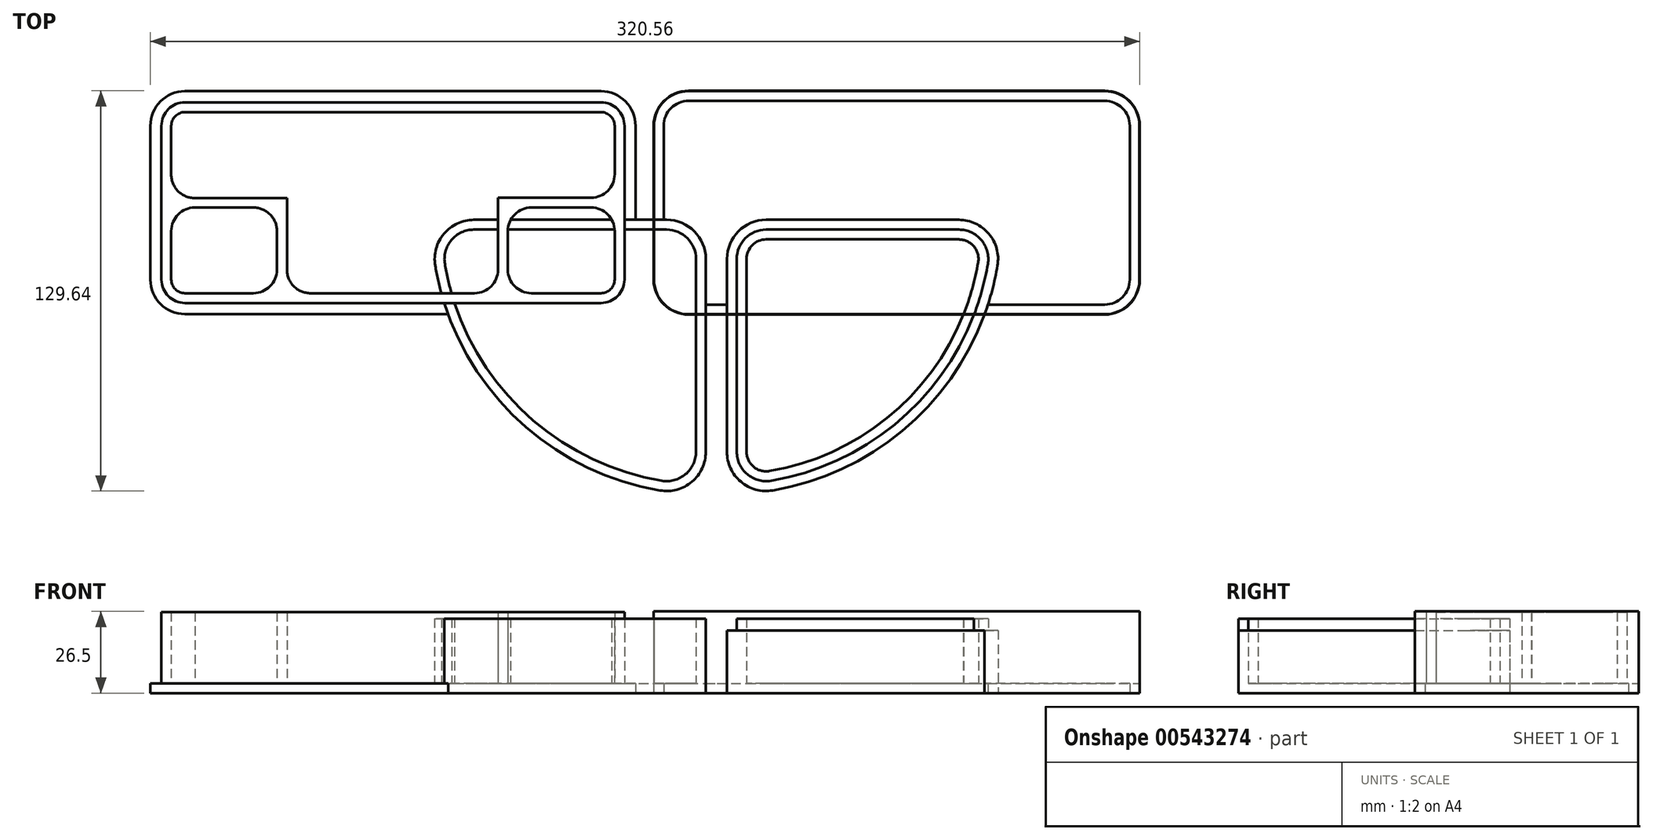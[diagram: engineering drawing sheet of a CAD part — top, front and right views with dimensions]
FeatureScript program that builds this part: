
annotation { "Feature Type Name" : "Feature", "Feature Type Description" : "" }
export const myFeature = defineFeature(function(context is Context, id is Id, definition is map)
    precondition{}
    {
        {
            var Q0;
            Q0=qCreatedBy(makeId("Top.planeOp"),FACE);
            var sketch = newSketch(context, id + "F0", { "sketchPlane" : qUnion([Q0])});
            skLineSegment(sketch, "E0.bottom", {"start": v(10.47, 17.5) * mm, "end": v(-124.29, 17.5) * mm});
            skLineSegment(sketch, "E0.top", {"start": v(10.47, 82.5) * mm, "end": v(-124.29, 82.5) * mm});
            skLineSegment(sketch, "E0.left", {"start": v(18.1, 25.13) * mm, "end": v(18.1, 74.89) * mm});
            skLineSegment(sketch, "E0.right", {"start": v(-131.9, 25.13) * mm, "end": v(-131.9, 74.89) * mm});
            skPoint(sketch, "E0.middle", {"position": v(-56.9, 50) * mm});
            skPoint(sketch, "E1.visualSharp", {"position": v(-131.9, 82.5) * mm});
            skArc(sketch, "E1.filletArc", {"start": v(-124.29, 82.5) * mm, "mid": v(-129.68, 80.28) * mm, "end": v(-131.9, 74.89) * mm});
            skPoint(sketch, "E2.visualSharp", {"position": v(-131.9, 17.5) * mm});
            skArc(sketch, "E2.filletArc", {"start": v(-131.9, 25.13) * mm, "mid": v(-129.68, 19.74) * mm, "end": v(-124.29, 17.5) * mm});
            skPoint(sketch, "E3.visualSharp", {"position": v(18.1, 17.5) * mm});
            skArc(sketch, "E3.filletArc", {"start": v(10.47, 17.5) * mm, "mid": v(15.86, 19.74) * mm, "end": v(18.1, 25.13) * mm});
            skPoint(sketch, "E4.visualSharp", {"position": v(18.1, 82.5) * mm});
            skArc(sketch, "E4.filletArc", {"start": v(18.1, 74.89) * mm, "mid": v(15.86, 80.28) * mm, "end": v(10.47, 82.5) * mm});
            skArc(sketch, "E5.0", {"start": v(14.92, 74.89) * mm, "mid": v(13.61, 78.03) * mm, "end": v(10.47, 79.33) * mm});
            skLineSegment(sketch, "E5.1", {"start": v(14.92, 59.22) * mm, "end": v(14.92, 74.89) * mm});
            skLineSegment(sketch, "E5.2", {"start": v(10.47, 79.33) * mm, "end": v(-124.29, 79.33) * mm});
            skArc(sketch, "E5.3", {"start": v(10.47, 20.68) * mm, "mid": v(13.61, 21.98) * mm, "end": v(14.92, 25.13) * mm});
            skArc(sketch, "E5.4", {"start": v(-124.29, 79.33) * mm, "mid": v(-127.43, 78.03) * mm, "end": v(-128.73, 74.89) * mm});
            skLineSegment(sketch, "E5.5", {"start": v(-128.73, 59.11) * mm, "end": v(-128.73, 74.89) * mm});
            skArc(sketch, "E5.6", {"start": v(-128.73, 25.13) * mm, "mid": v(-127.43, 21.98) * mm, "end": v(-124.29, 20.68) * mm});
            skLineSegment(sketch, "E5.7", {"start": v(-30.47, 20.68) * mm, "end": v(-83.6, 20.68) * mm});
            skLineSegment(sketch, "E6.0", {"start": v(24.7, 25.13) * mm, "end": v(24.7, 74.89) * mm, "construction": true});
            skLineSegment(sketch, "E7.left", {"start": v(14.92, 40.8) * mm, "end": v(14.92, 59.22) * mm});
            skLineSegment(sketch, "E7.right", {"start": v(-128.73, 49.97) * mm, "end": v(-128.73, 51.6) * mm});
            skPoint(sketch, "E8.newPointA", {"position": v(-128.73, 51.6) * mm});
            skPoint(sketch, "E8.newPointB", {"position": v(-128.73, 25.13) * mm});
            skArc(sketch, "E8.filletArc", {"start": v(-128.73, 59.11) * mm, "mid": v(-126.47, 53.7) * mm, "end": v(-121.01, 51.5) * mm});
            skPoint(sketch, "E9.newPointA", {"position": v(14.92, 51.6) * mm});
            skPoint(sketch, "E9.newPointB", {"position": v(14.92, 25.13) * mm});
            skArc(sketch, "E9.filletArc", {"start": v(7.3, 51.6) * mm, "mid": v(12.68, 53.83) * mm, "end": v(14.92, 59.22) * mm});
            skPoint(sketch, "E10.visualSharp", {"position": v(-128.73, 48.42) * mm});
            skLineSegment(sketch, "E11", {"start": v(-128.73, 25.13) * mm, "end": v(-128.73, 40.8) * mm});
            skLineSegment(sketch, "E12", {"start": v(14.92, 25.13) * mm, "end": v(14.92, 40.8) * mm});
            skArc(sketch, "E13.filletArc", {"start": v(-121.11, 48.42) * mm, "mid": v(-126.5, 46.19) * mm, "end": v(-128.73, 40.8) * mm});
            skPoint(sketch, "E14.visualSharp", {"position": v(14.92, 48.42) * mm});
            skArc(sketch, "E14.filletArc", {"start": v(14.92, 40.8) * mm, "mid": v(12.68, 46.19) * mm, "end": v(7.3, 48.42) * mm});
            skLineSegment(sketch, "E15", {"start": v(-128.73, 59.11) * mm, "end": v(-128.73, 40.8) * mm});
            skArc(sketch, "E16.0", {"start": v(27.55, 74.89) * mm, "mid": v(30.88, 82.93) * mm, "end": v(38.92, 86.26) * mm});
            skLineSegment(sketch, "E16.1", {"start": v(27.55, 25.13) * mm, "end": v(27.55, 74.89) * mm});
            skLineSegment(sketch, "E16.2", {"start": v(38.92, 86.26) * mm, "end": v(173.68, 86.26) * mm});
            skArc(sketch, "E16.3", {"start": v(38.92, 13.76) * mm, "mid": v(30.88, 17.09) * mm, "end": v(27.55, 25.13) * mm});
            skArc(sketch, "E16.4", {"start": v(173.68, 86.26) * mm, "mid": v(181.72, 82.93) * mm, "end": v(185.05, 74.89) * mm});
            skLineSegment(sketch, "E16.5", {"start": v(185.05, 25.13) * mm, "end": v(185.05, 74.89) * mm});
            skArc(sketch, "E16.6", {"start": v(185.05, 25.13) * mm, "mid": v(181.72, 17.09) * mm, "end": v(173.68, 13.76) * mm});
            skLineSegment(sketch, "E16.7", {"start": v(38.92, 13.76) * mm, "end": v(173.68, 13.76) * mm});
            skArc(sketch, "E17.0", {"start": v(27.65, 74.89) * mm, "mid": v(30.95, 82.86) * mm, "end": v(38.92, 86.16) * mm});
            skLineSegment(sketch, "E17.1", {"start": v(27.65, 25.13) * mm, "end": v(27.65, 74.89) * mm});
            skLineSegment(sketch, "E17.2", {"start": v(38.92, 86.16) * mm, "end": v(173.68, 86.16) * mm});
            skArc(sketch, "E17.3", {"start": v(38.92, 13.86) * mm, "mid": v(30.95, 17.16) * mm, "end": v(27.65, 25.13) * mm});
            skArc(sketch, "E17.4", {"start": v(173.68, 86.16) * mm, "mid": v(181.65, 82.86) * mm, "end": v(184.95, 74.89) * mm});
            skLineSegment(sketch, "E17.5", {"start": v(184.95, 25.13) * mm, "end": v(184.95, 74.89) * mm});
            skArc(sketch, "E17.6", {"start": v(184.95, 25.13) * mm, "mid": v(181.65, 17.16) * mm, "end": v(173.68, 13.86) * mm});
            skLineSegment(sketch, "E17.7", {"start": v(38.92, 13.86) * mm, "end": v(173.68, 13.86) * mm});
            skArc(sketch, "E18.0", {"start": v(30.8, 74.89) * mm, "mid": v(33.18, 80.63) * mm, "end": v(38.92, 83) * mm});
            skLineSegment(sketch, "E18.1", {"start": v(30.8, 25.13) * mm, "end": v(30.8, 74.89) * mm});
            skLineSegment(sketch, "E18.2", {"start": v(38.92, 83) * mm, "end": v(173.68, 83) * mm});
            skArc(sketch, "E18.3", {"start": v(38.92, 17) * mm, "mid": v(33.18, 19.39) * mm, "end": v(30.8, 25.13) * mm});
            skArc(sketch, "E18.4", {"start": v(173.68, 83) * mm, "mid": v(179.42, 80.63) * mm, "end": v(181.8, 74.89) * mm});
            skLineSegment(sketch, "E18.5", {"start": v(181.8, 25.13) * mm, "end": v(181.8, 74.89) * mm});
            skArc(sketch, "E18.6", {"start": v(181.8, 25.13) * mm, "mid": v(179.42, 19.39) * mm, "end": v(173.68, 17) * mm});
            skLineSegment(sketch, "E18.7", {"start": v(38.92, 17) * mm, "end": v(173.68, 17) * mm});
            skLineSegment(sketch, "E19.1.0.0", {"start": v(-94.5, 28.3) * mm, "end": v(-94.48, 40.79) * mm});
            skPoint(sketch, "E20.orphan", {"position": v(-92.9, 40.77) * mm});
            skPoint(sketch, "E21.orphan", {"position": v(-57.07, 40.74) * mm});
            skPoint(sketch, "E22.orphan", {"position": v(-21.23, 40.72) * mm});
            skPoint(sketch, "E23.orphan", {"position": v(-21.23, 25.04) * mm});
            skPoint(sketch, "E24.orphan", {"position": v(-57.07, 25.07) * mm});
            skArc(sketch, "E25.filletArc", {"start": v(-91.23, 28.32) * mm, "mid": v(-89, 22.92) * mm, "end": v(-83.6, 20.68) * mm});
            skArc(sketch, "E26.filletArc", {"start": v(-30.47, 20.68) * mm, "mid": v(-25.08, 22.91) * mm, "end": v(-22.85, 28.3) * mm});
            skLineSegment(sketch, "E27", {"start": v(-124.29, 20.68) * mm, "end": v(-102.12, 20.68) * mm});
            skLineSegment(sketch, "E28", {"start": v(-12.05, 20.68) * mm, "end": v(10.47, 20.68) * mm});
            skLineSegment(sketch, "E29", {"start": v(-12.05, 48.42) * mm, "end": v(7.3, 48.42) * mm});
            skPoint(sketch, "E30.visualSharp", {"position": v(-19.67, 48.42) * mm});
            skArc(sketch, "E30.filletArc", {"start": v(-12.05, 48.42) * mm, "mid": v(-17.44, 46.19) * mm, "end": v(-19.67, 40.8) * mm});
            skPoint(sketch, "E31.visualSharp", {"position": v(-19.67, 20.68) * mm});
            skArc(sketch, "E31.filletArc", {"start": v(-19.67, 28.3) * mm, "mid": v(-17.44, 22.91) * mm, "end": v(-12.05, 20.68) * mm});
            skPoint(sketch, "E32.visualSharp", {"position": v(-94.51, 20.68) * mm});
            skArc(sketch, "E32.filletArc", {"start": v(-102.12, 20.68) * mm, "mid": v(-96.74, 22.91) * mm, "end": v(-94.5, 28.3) * mm});
            skLineSegment(sketch, "E33", {"start": v(-121.11, 48.42) * mm, "end": v(-102.1, 48.42) * mm});
            skArc(sketch, "E34.filletArc", {"start": v(-94.48, 40.79) * mm, "mid": v(-96.7, 46.18) * mm, "end": v(-102.1, 48.42) * mm});
            skLineSegment(sketch, "E35", {"start": v(7.3, 51.6) * mm, "end": v(-121.01, 51.5) * mm});
            skLineSegment(sketch, "E36", {"start": v(-22.85, 28.3) * mm, "end": v(-22.87, 51.57) * mm});
            skLineSegment(sketch, "E37", {"start": v(-91.23, 28.32) * mm, "end": v(-91.24, 51.52) * mm});
            skLineSegment(sketch, "E38", {"start": v(-19.67, 28.3) * mm, "end": v(-19.67, 40.8) * mm});
            skLineSegment(sketch, "E39", {"start": v(42.8, 86.16) * mm, "end": v(-129, 86.16) * mm, "construction": true});
            skArc(sketch, "E40.0", {"start": v(21.7, 74.89) * mm, "mid": v(18.4, 82.82) * mm, "end": v(10.47, 86.1) * mm});
            skLineSegment(sketch, "E40.1", {"start": v(21.7, 25.13) * mm, "end": v(21.7, 74.89) * mm});
            skLineSegment(sketch, "E40.2", {"start": v(10.47, 86.1) * mm, "end": v(-124.29, 86.1) * mm});
            skArc(sketch, "E40.3", {"start": v(10.47, 13.9) * mm, "mid": v(18.4, 17.2) * mm, "end": v(21.7, 25.13) * mm});
            skArc(sketch, "E40.4", {"start": v(-124.29, 86.1) * mm, "mid": v(-132.22, 82.82) * mm, "end": v(-135.5, 74.89) * mm});
            skLineSegment(sketch, "E40.5", {"start": v(-135.5, 25.13) * mm, "end": v(-135.5, 74.89) * mm});
            skArc(sketch, "E40.6", {"start": v(-135.5, 25.13) * mm, "mid": v(-132.22, 17.2) * mm, "end": v(-124.29, 13.9) * mm});
            skLineSegment(sketch, "E40.7", {"start": v(10.47, 13.9) * mm, "end": v(-124.29, 13.9) * mm});
            skSolve(sketch);
        }
        {
            var Q0;
            Q0=qCreatedBy(makeId("Top.planeOp"),FACE);
            var sketch = newSketch(context, id + "F1", { "sketchPlane" : qUnion([Q0])});
            skLineSegment(sketch, "E41.bottom", {"start": v(44.45, -44.45) * mm, "end": v(-44.45, -44.45) * mm});
            skLineSegment(sketch, "E41.top", {"start": v(31.75, 44.45) * mm, "end": v(-30.68, 44.45) * mm});
            skLineSegment(sketch, "E41.left", {"start": v(44.45, -30.68) * mm, "end": v(44.45, 31.75) * mm});
            skLineSegment(sketch, "E41.right", {"start": v(-44.45, -44.45) * mm, "end": v(-44.45, 44.45) * mm});
            skPoint(sketch, "E41.middle", {"position": v(0, 0) * mm});
            skLineSegment(sketch, "E42.0", {"start": v(47.88, -44.45) * mm, "end": v(47.88, 44.45) * mm, "construction": true});
            skArc(sketch, "E43", {"start": v(-43.2, 29.63) * mm, "mid": v(-18.41, -18.41) * mm, "end": v(29.63, -43.2) * mm});
            skPoint(sketch, "E44.visualSharp", {"position": v(-44.45, 44.45) * mm});
            skArc(sketch, "E44.filletArc", {"start": v(-30.68, 44.45) * mm, "mid": v(-40.38, 39.95) * mm, "end": v(-43.2, 29.63) * mm});
            skPoint(sketch, "E45.visualSharp", {"position": v(44.45, -44.45) * mm});
            skArc(sketch, "E45.filletArc", {"start": v(29.63, -43.2) * mm, "mid": v(39.95, -40.38) * mm, "end": v(44.45, -30.68) * mm});
            skArc(sketch, "E46.filletArc", {"start": v(44.45, 31.75) * mm, "mid": v(40.73, 40.73) * mm, "end": v(31.75, 44.45) * mm});
            skArc(sketch, "E47.0", {"start": v(41.28, 31.75) * mm, "mid": v(38.49, 38.49) * mm, "end": v(31.75, 41.27) * mm});
            skArc(sketch, "E47.1", {"start": v(-30.68, 41.27) * mm, "mid": v(-37.96, 37.9) * mm, "end": v(-40.08, 30.16) * mm});
            skArc(sketch, "E47.2", {"start": v(-40.08, 30.16) * mm, "mid": v(-16.17, -16.17) * mm, "end": v(30.16, -40.08) * mm});
            skLineSegment(sketch, "E47.3", {"start": v(31.75, 41.27) * mm, "end": v(-30.68, 41.27) * mm});
            skArc(sketch, "E47.4", {"start": v(30.16, -40.08) * mm, "mid": v(37.9, -37.96) * mm, "end": v(41.28, -30.68) * mm});
            skLineSegment(sketch, "E47.5", {"start": v(41.28, -30.68) * mm, "end": v(41.28, 31.75) * mm});
            skLineSegment(sketch, "E48.0", {"start": v(31.75, 38.1) * mm, "end": v(-30.68, 38.1) * mm});
            skArc(sketch, "E48.1", {"start": v(-36.95, 30.7) * mm, "mid": v(-13.92, -13.92) * mm, "end": v(30.7, -36.95) * mm});
            skArc(sketch, "E48.2", {"start": v(30.7, -36.95) * mm, "mid": v(35.85, -35.53) * mm, "end": v(38.1, -30.68) * mm});
            skArc(sketch, "E48.3", {"start": v(-30.68, 38.1) * mm, "mid": v(-35.53, 35.85) * mm, "end": v(-36.95, 30.7) * mm});
            skLineSegment(sketch, "E48.4", {"start": v(38.1, -30.68) * mm, "end": v(38.1, 31.75) * mm});
            skArc(sketch, "E48.5", {"start": v(38.1, 31.75) * mm, "mid": v(36.24, 36.24) * mm, "end": v(31.75, 38.1) * mm});
            skLineSegment(sketch, "E49.MirrorCS", {"start": v(51.3, -30.68) * mm, "end": v(51.3, 31.75) * mm});
            skLineSegment(sketch, "E50.MirrorCS", {"start": v(54.48, -30.68) * mm, "end": v(54.48, 31.75) * mm});
            skLineSegment(sketch, "E51.MirrorCS", {"start": v(57.66, -30.68) * mm, "end": v(57.66, 31.75) * mm});
            skArc(sketch, "E52.MirrorCS", {"start": v(57.66, 31.75) * mm, "mid": v(59.52, 36.24) * mm, "end": v(64, 38.1) * mm});
            skArc(sketch, "E53.MirrorCS", {"start": v(54.48, 31.75) * mm, "mid": v(57.27, 38.49) * mm, "end": v(64, 41.28) * mm});
            skArc(sketch, "E54.MirrorCS", {"start": v(51.3, 31.75) * mm, "mid": v(55.03, 40.73) * mm, "end": v(64, 44.45) * mm});
            skLineSegment(sketch, "E55.MirrorCS", {"start": v(64, 44.45) * mm, "end": v(126.44, 44.45) * mm});
            skLineSegment(sketch, "E56.MirrorCS", {"start": v(64, 41.27) * mm, "end": v(126.44, 41.27) * mm});
            skLineSegment(sketch, "E57.MirrorCS", {"start": v(64, 38.1) * mm, "end": v(126.44, 38.1) * mm});
            skArc(sketch, "E58.MirrorCS", {"start": v(126.44, 38.1) * mm, "mid": v(131.3, 35.85) * mm, "end": v(132.7, 30.7) * mm});
            skArc(sketch, "E59.MirrorCS", {"start": v(126.44, 41.28) * mm, "mid": v(133.72, 37.9) * mm, "end": v(135.83, 30.16) * mm});
            skArc(sketch, "E60.MirrorCS", {"start": v(126.44, 44.45) * mm, "mid": v(136.14, 39.95) * mm, "end": v(138.96, 29.63) * mm});
            skArc(sketch, "E61.MirrorCS", {"start": v(132.7, 30.7) * mm, "mid": v(109.68, -13.92) * mm, "end": v(65.07, -36.95) * mm});
            skArc(sketch, "E62.MirrorCS", {"start": v(135.83, 30.16) * mm, "mid": v(111.92, -16.17) * mm, "end": v(65.6, -40.08) * mm});
            skArc(sketch, "E63.MirrorCS", {"start": v(138.96, 29.63) * mm, "mid": v(114.17, -18.41) * mm, "end": v(66.12, -43.2) * mm});
            skArc(sketch, "E64.MirrorCS", {"start": v(66.12, -43.2) * mm, "mid": v(55.81, -40.38) * mm, "end": v(51.3, -30.68) * mm});
            skArc(sketch, "E65.MirrorCS", {"start": v(65.6, -40.08) * mm, "mid": v(57.86, -37.96) * mm, "end": v(54.48, -30.68) * mm});
            skArc(sketch, "E66.MirrorCS", {"start": v(65.07, -36.95) * mm, "mid": v(59.9, -35.53) * mm, "end": v(57.66, -30.68) * mm});
            skSolve(sketch);
        }
        {
            var Q0;
            Q0=makeQuery(id+"F1.imprint","IMPRINT",FACE,{"disambiguationData":[TD([[makeQuery(id+"F1.imprint","IMPRINT",EDGE,{"derivedFrom":sQuery(id+"F1.wireOp",EDGE,"E48.0")}),1.0]])]});
            var Q1;
            Q1=makeQuery(id+"F1.imprint","IMPRINT",FACE,{"disambiguationData":[TD([[makeQuery(id+"F1.imprint","IMPRINT",EDGE,{"derivedFrom":sQuery(id+"F1.wireOp",EDGE,"E47.0")}),1.0]])]});
            var Q2;
            Q2=makeQuery(id+"F1.imprint","IMPRINT",FACE,{"disambiguationData":[TD([[makeQuery(id+"F1.imprint","IMPRINT",EDGE,{"derivedFrom":sQuery(id+"F1.wireOp",EDGE,"E41.top")}),1.0]])]});
            var Q3;
            Q3=makeQuery(id+"F1.imprint","IMPRINT",FACE,{"disambiguationData":[TD([[makeQuery(id+"F1.imprint","IMPRINT",EDGE,{"derivedFrom":sQuery(id+"F1.wireOp",EDGE,"E49.MirrorCS")}),-1.0]])]});
            var Q4;
            Q4=makeQuery(id+"F1.imprint","IMPRINT",FACE,{"disambiguationData":[TD([[makeQuery(id+"F1.imprint","IMPRINT",EDGE,{"derivedFrom":sQuery(id+"F1.wireOp",EDGE,"E50.MirrorCS")}),-1.0]])]});
            var Q5;
            Q5=makeQuery(id+"F1.imprint","IMPRINT",FACE,{"disambiguationData":[TD([[makeQuery(id+"F1.imprint","IMPRINT",EDGE,{"derivedFrom":sQuery(id+"F1.wireOp",EDGE,"E51.MirrorCS")}),-1.0]])]});
            extrude(context, id + "F2", {"entities" : qUnion([Q0, Q1, Q2, Q3, Q4, Q5]), "depth" : 3.17 * mm, "offsetDistance" : 25.4 * mm});
        }
        {
            var Q0;
            Q0=makeQuery(id+"F1.imprint","IMPRINT",FACE,{"disambiguationData":[TD([[makeQuery(id+"F1.imprint","IMPRINT",EDGE,{"derivedFrom":sQuery(id+"F1.wireOp",EDGE,"E41.top")}),1.0]])]});
            extrude(context, id + "F3", {"entities" : qUnion([Q0]), "operationType" : NewBodyOperationType.ADD, "depth" : 24.13 * mm, "offsetDistance" : 25.4 * mm});
        }
        {
            var Q0;
            Q0=makeQuery(id+"F1.imprint","IMPRINT",FACE,{"disambiguationData":[TD([[makeQuery(id+"F1.imprint","IMPRINT",EDGE,{"derivedFrom":sQuery(id+"F1.wireOp",EDGE,"E49.MirrorCS")}),-1.0]])]});
            var Q1;
            Q1=makeQuery(id+"F1.imprint","IMPRINT",FACE,{"disambiguationData":[TD([[makeQuery(id+"F1.imprint","IMPRINT",EDGE,{"derivedFrom":sQuery(id+"F1.wireOp",EDGE,"E50.MirrorCS")}),-1.0]])]});
            extrude(context, id + "F4", {"entities" : qUnion([Q0, Q1]), "operationType" : NewBodyOperationType.ADD, "depth" : 20.32 * mm, "offsetDistance" : 25.4 * mm});
        }
        {
            var Q0;
            Q0=makeQuery(id+"F1.imprint","IMPRINT",FACE,{"disambiguationData":[TD([[makeQuery(id+"F1.imprint","IMPRINT",EDGE,{"derivedFrom":sQuery(id+"F1.wireOp",EDGE,"E50.MirrorCS")}),-1.0]])]});
            extrude(context, id + "F5", {"entities" : qUnion([Q0]), "operationType" : NewBodyOperationType.ADD, "depth" : 24.13 * mm, "offsetDistance" : 25.4 * mm});
        }
        {
            var Q0;
            Q0=makeQuery(id+"F0.imprint","IMPRINT",FACE,{"disambiguationData":[TD([[makeQuery(id+"F0.imprint","IMPRINT",EDGE,{"derivedFrom":sQuery(id+"F0.wireOp",EDGE,"E18.0")}),-1.0]])]});
            var Q1;
            Q1=makeQuery(id+"F0.imprint","IMPRINT",FACE,{"disambiguationData":[TD([[makeQuery(id+"F0.imprint","IMPRINT",EDGE,{"derivedFrom":sQuery(id+"F0.wireOp",EDGE,"E17.0")}),-1.0]])]});
            var Q2;
            Q2=makeQuery(id+"F0.imprint","IMPRINT",FACE,{"disambiguationData":[TD([[makeQuery(id+"F0.imprint","IMPRINT",EDGE,{"derivedFrom":sQuery(id+"F0.wireOp",EDGE,"E0.bottom")}),-1.0]])]});
            var Q3;
            Q3=makeQuery(id+"F0.imprint","IMPRINT",FACE,{"disambiguationData":[TD([[makeQuery(id+"F0.imprint","IMPRINT",EDGE,{"derivedFrom":sQuery(id+"F0.wireOp",EDGE,"E5.3")}),1.0]])]});
            var Q4;
            Q4=makeQuery(id+"F0.imprint","IMPRINT",FACE,{"disambiguationData":[TD([[makeQuery(id+"F0.imprint","IMPRINT",EDGE,{"derivedFrom":sQuery(id+"F0.wireOp",EDGE,"E7.bottom")}),-1.0]])]});
            var Q5;
            Q5=makeQuery(id+"F0.imprint","IMPRINT",FACE,{"disambiguationData":[TD([[makeQuery(id+"F0.imprint","IMPRINT",EDGE,{"derivedFrom":sQuery(id+"F0.wireOp",EDGE,"E5.0")}),1.0]])]});
            var Q6;
            Q6=makeQuery(id+"F0.imprint","IMPRINT",FACE,{"disambiguationData":[TD([[makeQuery(id+"F0.imprint","IMPRINT",EDGE,{"derivedFrom":sQuery(id+"F0.wireOp",EDGE,"E5.6")}),1.0]])]});
            var Q7;
            Q7=makeQuery(id+"F0.imprint","IMPRINT",FACE,{"disambiguationData":[TD([[makeQuery(id+"F0.imprint","IMPRINT",EDGE,{"derivedFrom":sQuery(id+"F0.wireOp",EDGE,"E5.7")}),-1.0]])]});
            extrude(context, id + "F6", {"entities" : qUnion([Q0, Q1, Q2, Q3, Q4, Q5, Q6, Q7]), "depth" : 3.17 * mm, "offsetDistance" : 25 * mm});
        }
        {
            var Q0;
            Q0=makeQuery(id+"F0.imprint","IMPRINT",FACE,{"disambiguationData":[TD([[makeQuery(id+"F0.imprint","IMPRINT",EDGE,{"derivedFrom":sQuery(id+"F0.wireOp",EDGE,"E0.bottom")}),-1.0]])]});
            var Q1;
            Q1=makeQuery(id+"F0.imprint","IMPRINT",FACE,{"disambiguationData":[TD([[makeQuery(id+"F0.imprint","IMPRINT",EDGE,{"derivedFrom":sQuery(id+"F0.wireOp",EDGE,"E7.bottom")}),-1.0]])]});
            extrude(context, id + "F7", {"entities" : qUnion([Q0, Q1]), "operationType" : NewBodyOperationType.ADD, "depth" : 26.27 * mm, "offsetDistance" : 25 * mm});
        }
        {
            var Q0;
            Q0=makeQuery(id+"F0.imprint","IMPRINT",FACE,{"disambiguationData":[TD([[makeQuery(id+"F0.imprint","IMPRINT",EDGE,{"derivedFrom":sQuery(id+"F0.wireOp",EDGE,"E17.0")}),-1.0]])]});
            extrude(context, id + "F8", {"entities" : qUnion([Q0]), "operationType" : NewBodyOperationType.ADD, "depth" : 26.5 * mm, "offsetDistance" : 25 * mm});
        }
        {
            var Q0;
            Q0=makeQuery(id+"F0.imprint","IMPRINT",FACE,{"disambiguationData":[TD([[makeQuery(id+"F0.imprint","IMPRINT",EDGE,{"derivedFrom":sQuery(id+"F0.wireOp",EDGE,"E0.bottom")}),1.0]])]});
            extrude(context, id + "F9", {"entities" : qUnion([Q0]), "operationType" : NewBodyOperationType.ADD, "depth" : 3.17 * mm, "offsetDistance" : 25 * mm});
        }
    });
